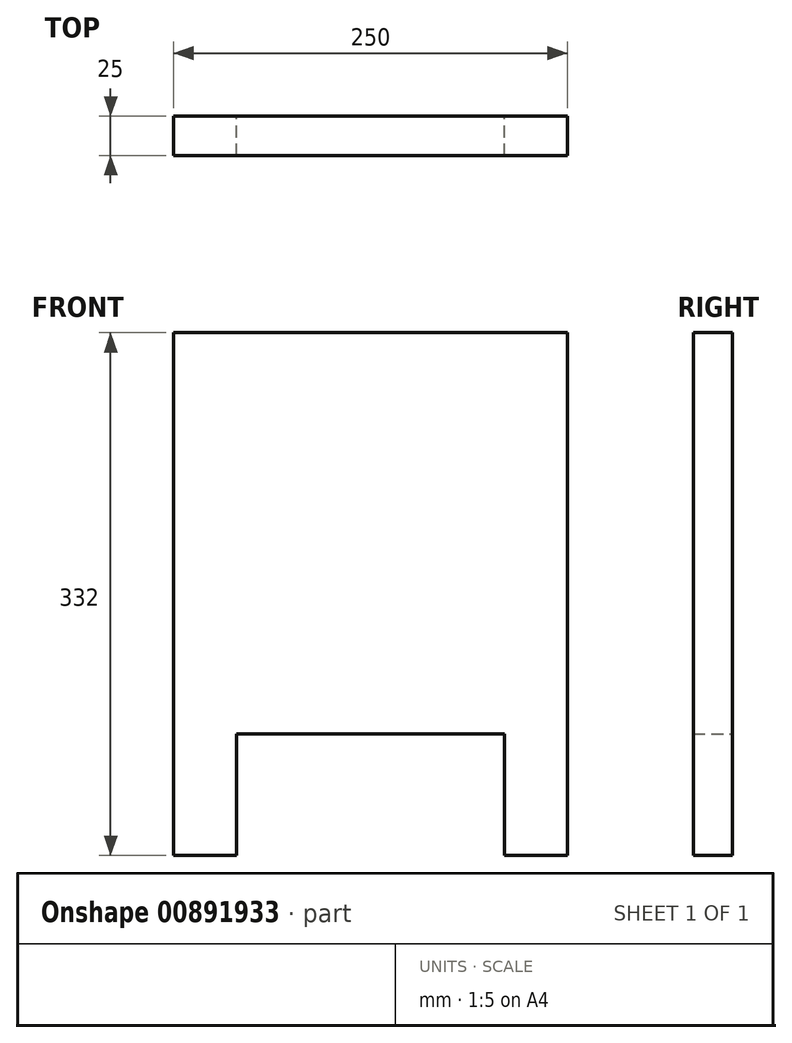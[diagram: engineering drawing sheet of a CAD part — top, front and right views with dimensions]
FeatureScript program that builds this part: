
annotation { "Feature Type Name" : "Feature", "Feature Type Description" : "" }
export const myFeature = defineFeature(function(context is Context, id is Id, definition is map)
    precondition{}
    {
        {
            var Q0;
            Q0=qCreatedBy(makeId("Front.planeOp"),FACE);
            var sketch = newSketch(context, id + "F0", { "sketchPlane" : qUnion([Q0])});
            skLineSegment(sketch, "E0.bottom", {"start": v(125, 166) * mm, "end": v(-125, 166) * mm});
            skLineSegment(sketch, "E0.top", {"start": v(125, -166) * mm, "end": v(85, -166) * mm});
            skLineSegment(sketch, "E0.left", {"start": v(125, 166) * mm, "end": v(125, -166) * mm});
            skLineSegment(sketch, "E0.right", {"start": v(-125, 166) * mm, "end": v(-125, -166) * mm});
            skPoint(sketch, "E0.middle", {"position": v(0, 0) * mm});
            skLineSegment(sketch, "E1.top", {"start": v(85, -89) * mm, "end": v(-85, -89) * mm});
            skLineSegment(sketch, "E1.left", {"start": v(85, -166) * mm, "end": v(85, -89) * mm});
            skLineSegment(sketch, "E1.right", {"start": v(-85, -166) * mm, "end": v(-85, -89) * mm});
            skPoint(sketch, "E1.middle", {"position": v(0, -127.5) * mm});
            skLineSegment(sketch, "E2.trimOffspring", {"start": v(-85, -166) * mm, "end": v(-125, -166) * mm});
            skSolve(sketch);
        }
        {
            var Q0;
            Q0 = qSketchRegion(id + "F0", true);
            extrude(context, id + "F1", {"entities" : qUnion([Q0]), "depth" : 25 * mm, "offsetDistance" : 25 * mm});
        }
    });
